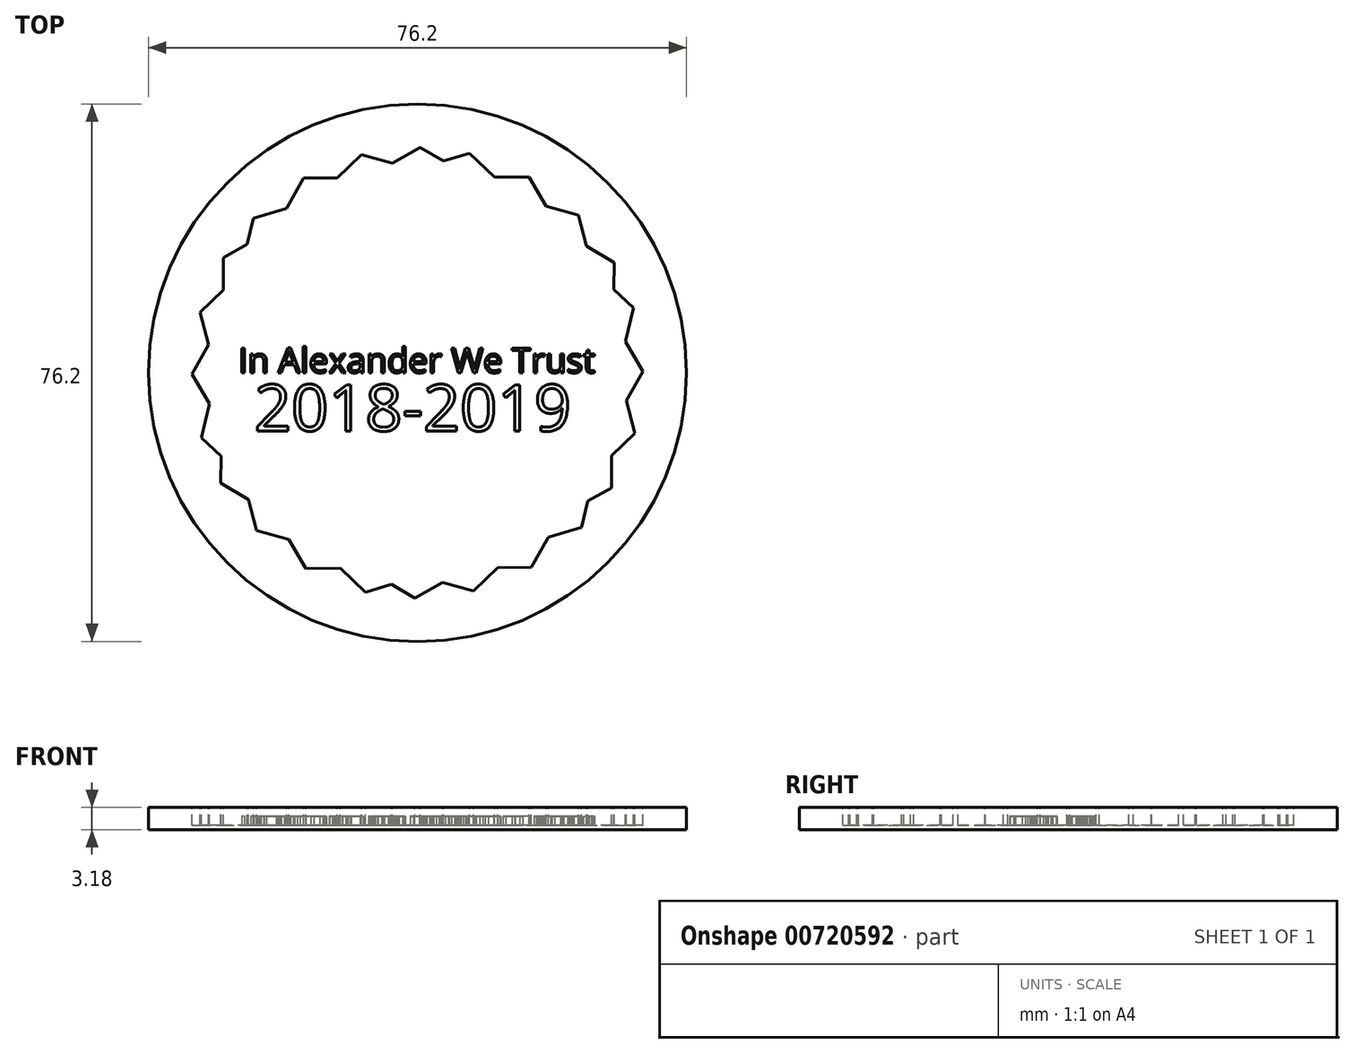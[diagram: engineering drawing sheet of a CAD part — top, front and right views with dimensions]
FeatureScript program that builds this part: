
annotation { "Feature Type Name" : "Feature", "Feature Type Description" : "" }
export const myFeature = defineFeature(function(context is Context, id is Id, definition is map)
    precondition{}
    {
        {
            var Q0;
            Q0=qCreatedBy(makeId("Top.planeOp"),FACE);
            var sketch = newSketch(context, id + "F0", { "sketchPlane" : qUnion([Q0])});
            skCircle(sketch, "E0", {"center": v(0, 0) * mm, "radius": 38.1 * mm});
            skSolve(sketch);
        }
        {
            var Q0;
            Q0=makeQuery(id+"F0.imprint","IMPRINT",FACE,{"disambiguationData":[TD([[makeQuery(id+"F0.imprint","IMPRINT",EDGE,{"derivedFrom":sQuery(id+"F0.wireOp",EDGE,"E0")}),1.0]])]});
            extrude(context, id + "F1", {"entities" : qUnion([Q0]), "depth" : 3.17 * mm, "offsetDistance" : 25.4 * mm});
        }
        {
            var Q0;
            Q0=makeQuery(id+"F1.opExtrude","CAP_FACE",FACE,{"disambiguationData":[OSD([sQuery(id+"F0.wireOp",EDGE,"E0")])],"isStart":false});
            var sketch = newSketch(context, id + "F2", { "sketchPlane" : qUnion([Q0])});
            skCircle(sketch, "E1", {"center": v(0, 0) * mm, "radius": 34.93 * mm});
            skCircle(sketch, "E2.cCircle", {"center": v(0, 0) * mm, "radius": 27.67 * mm, "construction": true});
            skLineSegment(sketch, "E2.0", {"start": v(15.83, 27.75) * mm, "end": v(31.95, 0.17) * mm});
            skLineSegment(sketch, "E2.1", {"start": v(31.95, 0.17) * mm, "end": v(16.12, -27.58) * mm});
            skLineSegment(sketch, "E2.2", {"start": v(16.12, -27.58) * mm, "end": v(-15.83, -27.75) * mm});
            skLineSegment(sketch, "E2.3", {"start": v(-15.83, -27.75) * mm, "end": v(-31.95, -0.17) * mm});
            skLineSegment(sketch, "E2.4", {"start": v(-31.95, -0.17) * mm, "end": v(-16.12, 27.58) * mm});
            skLineSegment(sketch, "E2.5", {"start": v(-16.12, 27.58) * mm, "end": v(15.83, 27.75) * mm});
            skPoint(sketch, "E2.0.midPoint", {"position": v(23.89, 13.96) * mm});
            skLineSegment(sketch, "E3.0", {"start": v(0.4, 31.95) * mm, "end": v(27.87, 15.63) * mm});
            skLineSegment(sketch, "E3.1", {"start": v(27.87, 15.63) * mm, "end": v(27.47, -16.32) * mm});
            skLineSegment(sketch, "E3.2", {"start": v(27.47, -16.32) * mm, "end": v(-0.4, -31.95) * mm});
            skLineSegment(sketch, "E3.3", {"start": v(-0.4, -31.95) * mm, "end": v(-27.87, -15.63) * mm});
            skLineSegment(sketch, "E3.4", {"start": v(-27.87, -15.63) * mm, "end": v(-27.47, 16.32) * mm});
            skLineSegment(sketch, "E3.5", {"start": v(-27.47, 16.32) * mm, "end": v(0.4, 31.95) * mm});
            skPoint(sketch, "E3.0.midPoint", {"position": v(14.13, 23.79) * mm});
            skLineSegment(sketch, "E4.0", {"start": v(22.82, 22.36) * mm, "end": v(30.78, -8.58) * mm});
            skLineSegment(sketch, "E4.1", {"start": v(30.78, -8.58) * mm, "end": v(7.96, -30.94) * mm});
            skLineSegment(sketch, "E4.2", {"start": v(7.96, -30.94) * mm, "end": v(-22.82, -22.36) * mm});
            skLineSegment(sketch, "E4.3", {"start": v(-22.82, -22.36) * mm, "end": v(-30.78, 8.58) * mm});
            skLineSegment(sketch, "E4.4", {"start": v(-30.78, 8.58) * mm, "end": v(-7.96, 30.94) * mm});
            skLineSegment(sketch, "E4.5", {"start": v(-7.96, 30.94) * mm, "end": v(22.82, 22.36) * mm});
            skPoint(sketch, "E4.0.midPoint", {"position": v(26.8, 6.9) * mm});
            skLineSegment(sketch, "E5.0", {"start": v(-23.26, 21.9) * mm, "end": v(7.34, 31.1) * mm});
            skLineSegment(sketch, "E5.1", {"start": v(7.34, 31.1) * mm, "end": v(30.6, 9.19) * mm});
            skLineSegment(sketch, "E5.2", {"start": v(30.6, 9.19) * mm, "end": v(23.26, -21.9) * mm});
            skLineSegment(sketch, "E5.3", {"start": v(23.26, -21.9) * mm, "end": v(-7.34, -31.1) * mm});
            skLineSegment(sketch, "E5.4", {"start": v(-7.34, -31.1) * mm, "end": v(-30.6, -9.19) * mm});
            skLineSegment(sketch, "E5.5", {"start": v(-30.6, -9.19) * mm, "end": v(-23.26, 21.9) * mm});
            skPoint(sketch, "E5.0.midPoint", {"position": v(-7.96, 26.5) * mm});
            skSolve(sketch);
        }
        {
            var Q0;
            {var subQ0=sQuery(id+"F2.wireOp",EDGE,"E4.2");var subQ1=sQuery(id+"F2.wireOp",EDGE,"E2.3");var subQ2=makeQuery(id+"F2.imprint","INTERSECT",VERTEX,{"derivedFrom":[subQ1,subQ0]});Q0=makeQuery(id+"F2.imprint","IMPRINT",FACE,{"disambiguationData":[TD([[makeQuery(id+"F2.imprint","IMPRINT",EDGE,{"disambiguationData":[TD([[subQ2,-1.0]])],"derivedFrom":subQ1}),-1.0]])]});}
            var Q1;
            {var subQ0=sQuery(id+"F2.wireOp",EDGE,"E2.3");var subQ1=sQuery(id+"F2.wireOp",EDGE,"E2.2");var subQ2=makeQuery(id+"F2.imprint","INTERSECT",VERTEX,{"derivedFrom":[subQ1,subQ0]});Q1=makeQuery(id+"F2.imprint","IMPRINT",FACE,{"disambiguationData":[TD([[makeQuery(id+"F2.imprint","IMPRINT",EDGE,{"disambiguationData":[TD([[subQ2,1.0]])],"derivedFrom":subQ1}),-1.0]])]});}
            var Q2;
            {var subQ0=sQuery(id+"F2.wireOp",EDGE,"E4.2");var subQ1=sQuery(id+"F2.wireOp",EDGE,"E2.2");var subQ2=makeQuery(id+"F2.imprint","INTERSECT",VERTEX,{"derivedFrom":[subQ1,subQ0]});Q2=makeQuery(id+"F2.imprint","IMPRINT",FACE,{"disambiguationData":[TD([[makeQuery(id+"F2.imprint","IMPRINT",EDGE,{"disambiguationData":[TD([[subQ2,-1.0]])],"derivedFrom":subQ1}),-1.0]])]});}
            var Q3;
            {var subQ0=sQuery(id+"F2.wireOp",EDGE,"E4.2");var subQ1=sQuery(id+"F2.wireOp",EDGE,"E2.2");var subQ2=makeQuery(id+"F2.imprint","INTERSECT",VERTEX,{"derivedFrom":[subQ1,subQ0]});Q3=makeQuery(id+"F2.imprint","IMPRINT",FACE,{"disambiguationData":[TD([[makeQuery(id+"F2.imprint","IMPRINT",EDGE,{"disambiguationData":[TD([[subQ2,-1.0]])],"derivedFrom":subQ1}),1.0]])]});}
            var Q4;
            {var subQ0=sQuery(id+"F2.wireOp",EDGE,"E3.2");var subQ1=sQuery(id+"F2.wireOp",EDGE,"E2.2");var subQ2=makeQuery(id+"F2.imprint","INTERSECT",VERTEX,{"derivedFrom":[subQ1,subQ0]});Q4=makeQuery(id+"F2.imprint","IMPRINT",FACE,{"disambiguationData":[TD([[makeQuery(id+"F2.imprint","IMPRINT",EDGE,{"disambiguationData":[TD([[subQ2,-1.0]])],"derivedFrom":subQ1}),1.0]])]});}
            var Q5;
            {var subQ0=sQuery(id+"F2.wireOp",EDGE,"E4.1");var subQ1=sQuery(id+"F2.wireOp",EDGE,"E2.2");var subQ2=makeQuery(id+"F2.imprint","INTERSECT",VERTEX,{"derivedFrom":[subQ1,subQ0]});Q5=makeQuery(id+"F2.imprint","IMPRINT",FACE,{"disambiguationData":[TD([[makeQuery(id+"F2.imprint","IMPRINT",EDGE,{"disambiguationData":[TD([[subQ2,-1.0]])],"derivedFrom":subQ1}),1.0]])]});}
            var Q6;
            {var subQ0=sQuery(id+"F2.wireOp",EDGE,"E4.1");var subQ1=sQuery(id+"F2.wireOp",EDGE,"E2.2");var subQ2=makeQuery(id+"F2.imprint","INTERSECT",VERTEX,{"derivedFrom":[subQ1,subQ0]});Q6=makeQuery(id+"F2.imprint","IMPRINT",FACE,{"disambiguationData":[TD([[makeQuery(id+"F2.imprint","IMPRINT",EDGE,{"disambiguationData":[TD([[subQ2,-1.0]])],"derivedFrom":subQ1}),-1.0]])]});}
            var Q7;
            {var subQ0=sQuery(id+"F2.wireOp",EDGE,"E2.2");var subQ1=sQuery(id+"F2.wireOp",EDGE,"E2.1");var subQ2=makeQuery(id+"F2.imprint","INTERSECT",VERTEX,{"derivedFrom":[subQ1,subQ0]});Q7=makeQuery(id+"F2.imprint","IMPRINT",FACE,{"disambiguationData":[TD([[makeQuery(id+"F2.imprint","IMPRINT",EDGE,{"disambiguationData":[TD([[subQ2,1.0]])],"derivedFrom":subQ1}),-1.0]])]});}
            var Q8;
            {var subQ15=sQuery(id+"F2.wireOp",EDGE,"E3.0");var subQ16=sQuery(id+"F2.wireOp",EDGE,"E2.0");var subQ17=makeQuery(id+"F2.imprint","INTERSECT",VERTEX,{"derivedFrom":[subQ16,subQ15]});Q8=makeQuery(id+"F2.imprint","IMPRINT",FACE,{"disambiguationData":[TD([[makeQuery(id+"F2.imprint","IMPRINT",EDGE,{"disambiguationData":[TD([[subQ17,-1.0]])],"derivedFrom":subQ16}),-1.0]])]});}
            var Q9;
            {var subQ0=sQuery(id+"F2.wireOp",EDGE,"E4.1");var subQ1=sQuery(id+"F2.wireOp",EDGE,"E2.1");var subQ2=makeQuery(id+"F2.imprint","INTERSECT",VERTEX,{"derivedFrom":[subQ1,subQ0]});Q9=makeQuery(id+"F2.imprint","IMPRINT",FACE,{"disambiguationData":[TD([[makeQuery(id+"F2.imprint","IMPRINT",EDGE,{"disambiguationData":[TD([[subQ2,-1.0]])],"derivedFrom":subQ1}),-1.0]])]});}
            var Q10;
            {var subQ0=sQuery(id+"F2.wireOp",EDGE,"E4.1");var subQ1=sQuery(id+"F2.wireOp",EDGE,"E2.1");var subQ2=makeQuery(id+"F2.imprint","INTERSECT",VERTEX,{"derivedFrom":[subQ1,subQ0]});Q10=makeQuery(id+"F2.imprint","IMPRINT",FACE,{"disambiguationData":[TD([[makeQuery(id+"F2.imprint","IMPRINT",EDGE,{"disambiguationData":[TD([[subQ2,-1.0]])],"derivedFrom":subQ1}),1.0]])]});}
            var Q11;
            {var subQ0=sQuery(id+"F2.wireOp",EDGE,"E3.1");var subQ1=sQuery(id+"F2.wireOp",EDGE,"E2.1");var subQ2=makeQuery(id+"F2.imprint","INTERSECT",VERTEX,{"derivedFrom":[subQ1,subQ0]});Q11=makeQuery(id+"F2.imprint","IMPRINT",FACE,{"disambiguationData":[TD([[makeQuery(id+"F2.imprint","IMPRINT",EDGE,{"disambiguationData":[TD([[subQ2,-1.0]])],"derivedFrom":subQ1}),1.0]])]});}
            var Q12;
            {var subQ0=sQuery(id+"F2.wireOp",EDGE,"E4.0");var subQ1=sQuery(id+"F2.wireOp",EDGE,"E2.1");var subQ2=makeQuery(id+"F2.imprint","INTERSECT",VERTEX,{"derivedFrom":[subQ1,subQ0]});Q12=makeQuery(id+"F2.imprint","IMPRINT",FACE,{"disambiguationData":[TD([[makeQuery(id+"F2.imprint","IMPRINT",EDGE,{"disambiguationData":[TD([[subQ2,-1.0]])],"derivedFrom":subQ1}),1.0]])]});}
            var Q13;
            {var subQ0=sQuery(id+"F2.wireOp",EDGE,"E4.0");var subQ1=sQuery(id+"F2.wireOp",EDGE,"E2.1");var subQ2=makeQuery(id+"F2.imprint","INTERSECT",VERTEX,{"derivedFrom":[subQ1,subQ0]});Q13=makeQuery(id+"F2.imprint","IMPRINT",FACE,{"disambiguationData":[TD([[makeQuery(id+"F2.imprint","IMPRINT",EDGE,{"disambiguationData":[TD([[subQ2,-1.0]])],"derivedFrom":subQ1}),-1.0]])]});}
            var Q14;
            {var subQ0=sQuery(id+"F2.wireOp",EDGE,"E2.1");var subQ1=sQuery(id+"F2.wireOp",EDGE,"E2.0");var subQ2=makeQuery(id+"F2.imprint","INTERSECT",VERTEX,{"derivedFrom":[subQ1,subQ0]});Q14=makeQuery(id+"F2.imprint","IMPRINT",FACE,{"disambiguationData":[TD([[makeQuery(id+"F2.imprint","IMPRINT",EDGE,{"disambiguationData":[TD([[subQ2,1.0]])],"derivedFrom":subQ1}),-1.0]])]});}
            var Q15;
            {var subQ0=sQuery(id+"F2.wireOp",EDGE,"E4.0");var subQ1=sQuery(id+"F2.wireOp",EDGE,"E2.0");var subQ2=makeQuery(id+"F2.imprint","INTERSECT",VERTEX,{"derivedFrom":[subQ1,subQ0]});Q15=makeQuery(id+"F2.imprint","IMPRINT",FACE,{"disambiguationData":[TD([[makeQuery(id+"F2.imprint","IMPRINT",EDGE,{"disambiguationData":[TD([[subQ2,-1.0]])],"derivedFrom":subQ1}),-1.0]])]});}
            var Q16;
            {var subQ0=sQuery(id+"F2.wireOp",EDGE,"E4.0");var subQ1=sQuery(id+"F2.wireOp",EDGE,"E2.0");var subQ2=makeQuery(id+"F2.imprint","INTERSECT",VERTEX,{"derivedFrom":[subQ1,subQ0]});Q16=makeQuery(id+"F2.imprint","IMPRINT",FACE,{"disambiguationData":[TD([[makeQuery(id+"F2.imprint","IMPRINT",EDGE,{"disambiguationData":[TD([[subQ2,-1.0]])],"derivedFrom":subQ1}),1.0]])]});}
            var Q17;
            {var subQ0=sQuery(id+"F2.wireOp",EDGE,"E3.0");var subQ1=sQuery(id+"F2.wireOp",EDGE,"E2.0");var subQ2=makeQuery(id+"F2.imprint","INTERSECT",VERTEX,{"derivedFrom":[subQ1,subQ0]});Q17=makeQuery(id+"F2.imprint","IMPRINT",FACE,{"disambiguationData":[TD([[makeQuery(id+"F2.imprint","IMPRINT",EDGE,{"disambiguationData":[TD([[subQ2,-1.0]])],"derivedFrom":subQ1}),1.0]])]});}
            var Q18;
            {var subQ0=sQuery(id+"F2.wireOp",EDGE,"E4.5");var subQ1=sQuery(id+"F2.wireOp",EDGE,"E2.0");var subQ2=makeQuery(id+"F2.imprint","INTERSECT",VERTEX,{"derivedFrom":[subQ1,subQ0]});Q18=makeQuery(id+"F2.imprint","IMPRINT",FACE,{"disambiguationData":[TD([[makeQuery(id+"F2.imprint","IMPRINT",EDGE,{"disambiguationData":[TD([[subQ2,-1.0]])],"derivedFrom":subQ1}),1.0]])]});}
            var Q19;
            {var subQ0=sQuery(id+"F2.wireOp",EDGE,"E4.5");var subQ1=sQuery(id+"F2.wireOp",EDGE,"E2.0");var subQ2=makeQuery(id+"F2.imprint","INTERSECT",VERTEX,{"derivedFrom":[subQ1,subQ0]});Q19=makeQuery(id+"F2.imprint","IMPRINT",FACE,{"disambiguationData":[TD([[makeQuery(id+"F2.imprint","IMPRINT",EDGE,{"disambiguationData":[TD([[subQ2,-1.0]])],"derivedFrom":subQ1}),-1.0]])]});}
            var Q20;
            {var subQ0=sQuery(id+"F2.wireOp",EDGE,"E2.5");var subQ1=sQuery(id+"F2.wireOp",EDGE,"E2.0");var subQ2=makeQuery(id+"F2.imprint","INTERSECT",VERTEX,{"derivedFrom":[subQ1,subQ0]});Q20=makeQuery(id+"F2.imprint","IMPRINT",FACE,{"disambiguationData":[TD([[makeQuery(id+"F2.imprint","IMPRINT",EDGE,{"disambiguationData":[TD([[subQ2,-1.0]])],"derivedFrom":subQ1}),-1.0]])]});}
            var Q21;
            {var subQ0=sQuery(id+"F2.wireOp",EDGE,"E4.5");var subQ1=sQuery(id+"F2.wireOp",EDGE,"E2.5");var subQ2=makeQuery(id+"F2.imprint","INTERSECT",VERTEX,{"derivedFrom":[subQ1,subQ0]});Q21=makeQuery(id+"F2.imprint","IMPRINT",FACE,{"disambiguationData":[TD([[makeQuery(id+"F2.imprint","IMPRINT",EDGE,{"disambiguationData":[TD([[subQ2,-1.0]])],"derivedFrom":subQ1}),1.0]])]});}
            var Q22;
            {var subQ0=sQuery(id+"F2.wireOp",EDGE,"E3.5");var subQ1=sQuery(id+"F2.wireOp",EDGE,"E2.5");var subQ2=makeQuery(id+"F2.imprint","INTERSECT",VERTEX,{"derivedFrom":[subQ1,subQ0]});Q22=makeQuery(id+"F2.imprint","IMPRINT",FACE,{"disambiguationData":[TD([[makeQuery(id+"F2.imprint","IMPRINT",EDGE,{"disambiguationData":[TD([[subQ2,-1.0]])],"derivedFrom":subQ1}),1.0]])]});}
            var Q23;
            {var subQ0=sQuery(id+"F2.wireOp",EDGE,"E4.5");var subQ1=sQuery(id+"F2.wireOp",EDGE,"E2.5");var subQ2=makeQuery(id+"F2.imprint","INTERSECT",VERTEX,{"derivedFrom":[subQ1,subQ0]});Q23=makeQuery(id+"F2.imprint","IMPRINT",FACE,{"disambiguationData":[TD([[makeQuery(id+"F2.imprint","IMPRINT",EDGE,{"disambiguationData":[TD([[subQ2,-1.0]])],"derivedFrom":subQ1}),-1.0]])]});}
            var Q24;
            {var subQ0=sQuery(id+"F2.wireOp",EDGE,"E4.4");var subQ1=sQuery(id+"F2.wireOp",EDGE,"E2.5");var subQ2=makeQuery(id+"F2.imprint","INTERSECT",VERTEX,{"derivedFrom":[subQ1,subQ0]});Q24=makeQuery(id+"F2.imprint","IMPRINT",FACE,{"disambiguationData":[TD([[makeQuery(id+"F2.imprint","IMPRINT",EDGE,{"disambiguationData":[TD([[subQ2,-1.0]])],"derivedFrom":subQ1}),-1.0]])]});}
            var Q25;
            {var subQ0=sQuery(id+"F2.wireOp",EDGE,"E4.4");var subQ1=sQuery(id+"F2.wireOp",EDGE,"E2.5");var subQ2=makeQuery(id+"F2.imprint","INTERSECT",VERTEX,{"derivedFrom":[subQ1,subQ0]});Q25=makeQuery(id+"F2.imprint","IMPRINT",FACE,{"disambiguationData":[TD([[makeQuery(id+"F2.imprint","IMPRINT",EDGE,{"disambiguationData":[TD([[subQ2,-1.0]])],"derivedFrom":subQ1}),1.0]])]});}
            var Q26;
            {var subQ0=sQuery(id+"F2.wireOp",EDGE,"E2.5");var subQ1=sQuery(id+"F2.wireOp",EDGE,"E2.4");var subQ2=makeQuery(id+"F2.imprint","INTERSECT",VERTEX,{"derivedFrom":[subQ1,subQ0]});Q26=makeQuery(id+"F2.imprint","IMPRINT",FACE,{"disambiguationData":[TD([[makeQuery(id+"F2.imprint","IMPRINT",EDGE,{"disambiguationData":[TD([[subQ2,1.0]])],"derivedFrom":subQ1}),-1.0]])]});}
            var Q27;
            {var subQ0=sQuery(id+"F2.wireOp",EDGE,"E4.4");var subQ1=sQuery(id+"F2.wireOp",EDGE,"E2.4");var subQ2=makeQuery(id+"F2.imprint","INTERSECT",VERTEX,{"derivedFrom":[subQ1,subQ0]});Q27=makeQuery(id+"F2.imprint","IMPRINT",FACE,{"disambiguationData":[TD([[makeQuery(id+"F2.imprint","IMPRINT",EDGE,{"disambiguationData":[TD([[subQ2,-1.0]])],"derivedFrom":subQ1}),-1.0]])]});}
            var Q28;
            {var subQ0=sQuery(id+"F2.wireOp",EDGE,"E4.4");var subQ1=sQuery(id+"F2.wireOp",EDGE,"E2.4");var subQ2=makeQuery(id+"F2.imprint","INTERSECT",VERTEX,{"derivedFrom":[subQ1,subQ0]});Q28=makeQuery(id+"F2.imprint","IMPRINT",FACE,{"disambiguationData":[TD([[makeQuery(id+"F2.imprint","IMPRINT",EDGE,{"disambiguationData":[TD([[subQ2,-1.0]])],"derivedFrom":subQ1}),1.0]])]});}
            var Q29;
            {var subQ0=sQuery(id+"F2.wireOp",EDGE,"E3.4");var subQ1=sQuery(id+"F2.wireOp",EDGE,"E2.4");var subQ2=makeQuery(id+"F2.imprint","INTERSECT",VERTEX,{"derivedFrom":[subQ1,subQ0]});Q29=makeQuery(id+"F2.imprint","IMPRINT",FACE,{"disambiguationData":[TD([[makeQuery(id+"F2.imprint","IMPRINT",EDGE,{"disambiguationData":[TD([[subQ2,-1.0]])],"derivedFrom":subQ1}),1.0]])]});}
            var Q30;
            {var subQ0=sQuery(id+"F2.wireOp",EDGE,"E4.3");var subQ1=sQuery(id+"F2.wireOp",EDGE,"E2.4");var subQ2=makeQuery(id+"F2.imprint","INTERSECT",VERTEX,{"derivedFrom":[subQ1,subQ0]});Q30=makeQuery(id+"F2.imprint","IMPRINT",FACE,{"disambiguationData":[TD([[makeQuery(id+"F2.imprint","IMPRINT",EDGE,{"disambiguationData":[TD([[subQ2,-1.0]])],"derivedFrom":subQ1}),1.0]])]});}
            var Q31;
            {var subQ0=sQuery(id+"F2.wireOp",EDGE,"E4.3");var subQ1=sQuery(id+"F2.wireOp",EDGE,"E2.4");var subQ2=makeQuery(id+"F2.imprint","INTERSECT",VERTEX,{"derivedFrom":[subQ1,subQ0]});Q31=makeQuery(id+"F2.imprint","IMPRINT",FACE,{"disambiguationData":[TD([[makeQuery(id+"F2.imprint","IMPRINT",EDGE,{"disambiguationData":[TD([[subQ2,-1.0]])],"derivedFrom":subQ1}),-1.0]])]});}
            var Q32;
            {var subQ0=sQuery(id+"F2.wireOp",EDGE,"E2.4");var subQ1=sQuery(id+"F2.wireOp",EDGE,"E2.3");var subQ2=makeQuery(id+"F2.imprint","INTERSECT",VERTEX,{"derivedFrom":[subQ1,subQ0]});Q32=makeQuery(id+"F2.imprint","IMPRINT",FACE,{"disambiguationData":[TD([[makeQuery(id+"F2.imprint","IMPRINT",EDGE,{"disambiguationData":[TD([[subQ2,1.0]])],"derivedFrom":subQ1}),-1.0]])]});}
            var Q33;
            {var subQ0=sQuery(id+"F2.wireOp",EDGE,"E4.3");var subQ1=sQuery(id+"F2.wireOp",EDGE,"E2.3");var subQ2=makeQuery(id+"F2.imprint","INTERSECT",VERTEX,{"derivedFrom":[subQ1,subQ0]});Q33=makeQuery(id+"F2.imprint","IMPRINT",FACE,{"disambiguationData":[TD([[makeQuery(id+"F2.imprint","IMPRINT",EDGE,{"disambiguationData":[TD([[subQ2,-1.0]])],"derivedFrom":subQ1}),-1.0]])]});}
            var Q34;
            {var subQ0=sQuery(id+"F2.wireOp",EDGE,"E3.3");var subQ1=sQuery(id+"F2.wireOp",EDGE,"E2.3");var subQ2=makeQuery(id+"F2.imprint","INTERSECT",VERTEX,{"derivedFrom":[subQ1,subQ0]});Q34=makeQuery(id+"F2.imprint","IMPRINT",FACE,{"disambiguationData":[TD([[makeQuery(id+"F2.imprint","IMPRINT",EDGE,{"disambiguationData":[TD([[subQ2,-1.0]])],"derivedFrom":subQ1}),1.0]])]});}
            var Q35;
            {var subQ0=sQuery(id+"F2.wireOp",EDGE,"E4.3");var subQ1=sQuery(id+"F2.wireOp",EDGE,"E2.3");var subQ2=makeQuery(id+"F2.imprint","INTERSECT",VERTEX,{"derivedFrom":[subQ1,subQ0]});Q35=makeQuery(id+"F2.imprint","IMPRINT",FACE,{"disambiguationData":[TD([[makeQuery(id+"F2.imprint","IMPRINT",EDGE,{"disambiguationData":[TD([[subQ2,-1.0]])],"derivedFrom":subQ1}),1.0]])]});}
            var Q36;
            {var subQ0=sQuery(id+"F2.wireOp",EDGE,"E3.4");var subQ1=sQuery(id+"F2.wireOp",EDGE,"E3.3");var subQ2=makeQuery(id+"F2.imprint","INTERSECT",VERTEX,{"derivedFrom":[subQ1,subQ0]});Q36=makeQuery(id+"F2.imprint","IMPRINT",FACE,{"disambiguationData":[TD([[makeQuery(id+"F2.imprint","IMPRINT",EDGE,{"disambiguationData":[TD([[subQ2,1.0]])],"derivedFrom":subQ1}),-1.0]])]});}
            var Q37;
            {var subQ0=sQuery(id+"F2.wireOp",EDGE,"E3.4");var subQ1=sQuery(id+"F2.wireOp",EDGE,"E2.3");var subQ2=makeQuery(id+"F2.imprint","INTERSECT",VERTEX,{"derivedFrom":[subQ1,subQ0]});Q37=makeQuery(id+"F2.imprint","IMPRINT",FACE,{"disambiguationData":[TD([[makeQuery(id+"F2.imprint","IMPRINT",EDGE,{"disambiguationData":[TD([[subQ2,-1.0]])],"derivedFrom":subQ1}),1.0]])]});}
            var Q38;
            {var subQ0=sQuery(id+"F2.wireOp",EDGE,"E3.4");var subQ1=sQuery(id+"F2.wireOp",EDGE,"E2.3");var subQ2=makeQuery(id+"F2.imprint","INTERSECT",VERTEX,{"derivedFrom":[subQ1,subQ0]});Q38=makeQuery(id+"F2.imprint","IMPRINT",FACE,{"disambiguationData":[TD([[makeQuery(id+"F2.imprint","IMPRINT",EDGE,{"disambiguationData":[TD([[subQ2,-1.0]])],"derivedFrom":subQ1}),-1.0]])]});}
            var Q39;
            {var subQ0=sQuery(id+"F2.wireOp",EDGE,"E4.3");var subQ1=sQuery(id+"F2.wireOp",EDGE,"E3.4");var subQ2=makeQuery(id+"F2.imprint","INTERSECT",VERTEX,{"derivedFrom":[subQ1,subQ0]});Q39=makeQuery(id+"F2.imprint","IMPRINT",FACE,{"disambiguationData":[TD([[makeQuery(id+"F2.imprint","IMPRINT",EDGE,{"disambiguationData":[TD([[subQ2,-1.0]])],"derivedFrom":subQ1}),1.0]])]});}
            var Q40;
            {var subQ0=sQuery(id+"F2.wireOp",EDGE,"E3.4");var subQ1=sQuery(id+"F2.wireOp",EDGE,"E2.4");var subQ2=makeQuery(id+"F2.imprint","INTERSECT",VERTEX,{"derivedFrom":[subQ1,subQ0]});Q40=makeQuery(id+"F2.imprint","IMPRINT",FACE,{"disambiguationData":[TD([[makeQuery(id+"F2.imprint","IMPRINT",EDGE,{"disambiguationData":[TD([[subQ2,-1.0]])],"derivedFrom":subQ1}),-1.0]])]});}
            var Q41;
            {var subQ0=sQuery(id+"F2.wireOp",EDGE,"E5.5");var subQ1=sQuery(id+"F2.wireOp",EDGE,"E2.4");var subQ2=makeQuery(id+"F2.imprint","INTERSECT",VERTEX,{"derivedFrom":[subQ1,subQ0]});Q41=makeQuery(id+"F2.imprint","IMPRINT",FACE,{"disambiguationData":[TD([[makeQuery(id+"F2.imprint","IMPRINT",EDGE,{"disambiguationData":[TD([[subQ2,-1.0]])],"derivedFrom":subQ1}),1.0]])]});}
            var Q42;
            {var subQ0=sQuery(id+"F2.wireOp",EDGE,"E3.5");var subQ1=sQuery(id+"F2.wireOp",EDGE,"E3.4");var subQ2=makeQuery(id+"F2.imprint","INTERSECT",VERTEX,{"derivedFrom":[subQ1,subQ0]});Q42=makeQuery(id+"F2.imprint","IMPRINT",FACE,{"disambiguationData":[TD([[makeQuery(id+"F2.imprint","IMPRINT",EDGE,{"disambiguationData":[TD([[subQ2,1.0]])],"derivedFrom":subQ1}),-1.0]])]});}
            var Q43;
            {var subQ0=sQuery(id+"F2.wireOp",EDGE,"E3.5");var subQ1=sQuery(id+"F2.wireOp",EDGE,"E2.4");var subQ2=makeQuery(id+"F2.imprint","INTERSECT",VERTEX,{"derivedFrom":[subQ1,subQ0]});Q43=makeQuery(id+"F2.imprint","IMPRINT",FACE,{"disambiguationData":[TD([[makeQuery(id+"F2.imprint","IMPRINT",EDGE,{"disambiguationData":[TD([[subQ2,-1.0]])],"derivedFrom":subQ1}),1.0]])]});}
            var Q44;
            {var subQ0=sQuery(id+"F2.wireOp",EDGE,"E3.0");var subQ1=sQuery(id+"F2.wireOp",EDGE,"E2.5");var subQ2=makeQuery(id+"F2.imprint","INTERSECT",VERTEX,{"derivedFrom":[subQ1,subQ0]});Q44=makeQuery(id+"F2.imprint","IMPRINT",FACE,{"disambiguationData":[TD([[makeQuery(id+"F2.imprint","IMPRINT",EDGE,{"disambiguationData":[TD([[subQ2,-1.0]])],"derivedFrom":subQ1}),1.0]])]});}
            var Q45;
            {var subQ0=sQuery(id+"F2.wireOp",EDGE,"E3.5");var subQ1=sQuery(id+"F2.wireOp",EDGE,"E3.0");var subQ2=makeQuery(id+"F2.imprint","INTERSECT",VERTEX,{"derivedFrom":[subQ1,subQ0]});Q45=makeQuery(id+"F2.imprint","IMPRINT",FACE,{"disambiguationData":[TD([[makeQuery(id+"F2.imprint","IMPRINT",EDGE,{"disambiguationData":[TD([[subQ2,-1.0]])],"derivedFrom":subQ1}),-1.0]])]});}
            var Q46;
            {var subQ0=sQuery(id+"F2.wireOp",EDGE,"E5.0");var subQ1=sQuery(id+"F2.wireOp",EDGE,"E2.5");var subQ2=makeQuery(id+"F2.imprint","INTERSECT",VERTEX,{"derivedFrom":[subQ1,subQ0]});Q46=makeQuery(id+"F2.imprint","IMPRINT",FACE,{"disambiguationData":[TD([[makeQuery(id+"F2.imprint","IMPRINT",EDGE,{"disambiguationData":[TD([[subQ2,-1.0]])],"derivedFrom":subQ1}),1.0]])]});}
            var Q47;
            {var subQ0=sQuery(id+"F2.wireOp",EDGE,"E3.5");var subQ1=sQuery(id+"F2.wireOp",EDGE,"E2.5");var subQ2=makeQuery(id+"F2.imprint","INTERSECT",VERTEX,{"derivedFrom":[subQ1,subQ0]});Q47=makeQuery(id+"F2.imprint","IMPRINT",FACE,{"disambiguationData":[TD([[makeQuery(id+"F2.imprint","IMPRINT",EDGE,{"disambiguationData":[TD([[subQ2,-1.0]])],"derivedFrom":subQ1}),-1.0]])]});}
            var Q48;
            {var subQ0=sQuery(id+"F2.wireOp",EDGE,"E3.5");var subQ1=sQuery(id+"F2.wireOp",EDGE,"E2.4");var subQ2=makeQuery(id+"F2.imprint","INTERSECT",VERTEX,{"derivedFrom":[subQ1,subQ0]});Q48=makeQuery(id+"F2.imprint","IMPRINT",FACE,{"disambiguationData":[TD([[makeQuery(id+"F2.imprint","IMPRINT",EDGE,{"disambiguationData":[TD([[subQ2,-1.0]])],"derivedFrom":subQ1}),-1.0]])]});}
            var Q49;
            {var subQ0=sQuery(id+"F2.wireOp",EDGE,"E3.1");var subQ1=sQuery(id+"F2.wireOp",EDGE,"E2.0");var subQ2=makeQuery(id+"F2.imprint","INTERSECT",VERTEX,{"derivedFrom":[subQ1,subQ0]});Q49=makeQuery(id+"F2.imprint","IMPRINT",FACE,{"disambiguationData":[TD([[makeQuery(id+"F2.imprint","IMPRINT",EDGE,{"disambiguationData":[TD([[subQ2,-1.0]])],"derivedFrom":subQ1}),1.0]])]});}
            var Q50;
            {var subQ0=sQuery(id+"F2.wireOp",EDGE,"E3.1");var subQ1=sQuery(id+"F2.wireOp",EDGE,"E3.0");var subQ2=makeQuery(id+"F2.imprint","INTERSECT",VERTEX,{"derivedFrom":[subQ1,subQ0]});Q50=makeQuery(id+"F2.imprint","IMPRINT",FACE,{"disambiguationData":[TD([[makeQuery(id+"F2.imprint","IMPRINT",EDGE,{"disambiguationData":[TD([[subQ2,1.0]])],"derivedFrom":subQ1}),-1.0]])]});}
            var Q51;
            {var subQ0=sQuery(id+"F2.wireOp",EDGE,"E3.1");var subQ1=sQuery(id+"F2.wireOp",EDGE,"E2.0");var subQ2=makeQuery(id+"F2.imprint","INTERSECT",VERTEX,{"derivedFrom":[subQ1,subQ0]});Q51=makeQuery(id+"F2.imprint","IMPRINT",FACE,{"disambiguationData":[TD([[makeQuery(id+"F2.imprint","IMPRINT",EDGE,{"disambiguationData":[TD([[subQ2,-1.0]])],"derivedFrom":subQ1}),-1.0]])]});}
            var Q52;
            {var subQ0=sQuery(id+"F2.wireOp",EDGE,"E3.2");var subQ1=sQuery(id+"F2.wireOp",EDGE,"E3.1");var subQ2=makeQuery(id+"F2.imprint","INTERSECT",VERTEX,{"derivedFrom":[subQ1,subQ0]});Q52=makeQuery(id+"F2.imprint","IMPRINT",FACE,{"disambiguationData":[TD([[makeQuery(id+"F2.imprint","IMPRINT",EDGE,{"disambiguationData":[TD([[subQ2,1.0]])],"derivedFrom":subQ1}),-1.0]])]});}
            var Q53;
            {var subQ0=sQuery(id+"F2.wireOp",EDGE,"E3.2");var subQ1=sQuery(id+"F2.wireOp",EDGE,"E2.1");var subQ2=makeQuery(id+"F2.imprint","INTERSECT",VERTEX,{"derivedFrom":[subQ1,subQ0]});Q53=makeQuery(id+"F2.imprint","IMPRINT",FACE,{"disambiguationData":[TD([[makeQuery(id+"F2.imprint","IMPRINT",EDGE,{"disambiguationData":[TD([[subQ2,-1.0]])],"derivedFrom":subQ1}),1.0]])]});}
            var Q54;
            {var subQ0=sQuery(id+"F2.wireOp",EDGE,"E3.2");var subQ1=sQuery(id+"F2.wireOp",EDGE,"E2.1");var subQ2=makeQuery(id+"F2.imprint","INTERSECT",VERTEX,{"derivedFrom":[subQ1,subQ0]});Q54=makeQuery(id+"F2.imprint","IMPRINT",FACE,{"disambiguationData":[TD([[makeQuery(id+"F2.imprint","IMPRINT",EDGE,{"disambiguationData":[TD([[subQ2,-1.0]])],"derivedFrom":subQ1}),-1.0]])]});}
            var Q55;
            {var subQ0=sQuery(id+"F2.wireOp",EDGE,"E3.3");var subQ1=sQuery(id+"F2.wireOp",EDGE,"E3.2");var subQ2=makeQuery(id+"F2.imprint","INTERSECT",VERTEX,{"derivedFrom":[subQ1,subQ0]});Q55=makeQuery(id+"F2.imprint","IMPRINT",FACE,{"disambiguationData":[TD([[makeQuery(id+"F2.imprint","IMPRINT",EDGE,{"disambiguationData":[TD([[subQ2,1.0]])],"derivedFrom":subQ1}),-1.0]])]});}
            var Q56;
            {var subQ0=sQuery(id+"F2.wireOp",EDGE,"E3.3");var subQ1=sQuery(id+"F2.wireOp",EDGE,"E2.2");var subQ2=makeQuery(id+"F2.imprint","INTERSECT",VERTEX,{"derivedFrom":[subQ1,subQ0]});Q56=makeQuery(id+"F2.imprint","IMPRINT",FACE,{"disambiguationData":[TD([[makeQuery(id+"F2.imprint","IMPRINT",EDGE,{"disambiguationData":[TD([[subQ2,-1.0]])],"derivedFrom":subQ1}),1.0]])]});}
            var Q57;
            {var subQ0=sQuery(id+"F2.wireOp",EDGE,"E3.3");var subQ1=sQuery(id+"F2.wireOp",EDGE,"E2.2");var subQ2=makeQuery(id+"F2.imprint","INTERSECT",VERTEX,{"derivedFrom":[subQ1,subQ0]});Q57=makeQuery(id+"F2.imprint","IMPRINT",FACE,{"disambiguationData":[TD([[makeQuery(id+"F2.imprint","IMPRINT",EDGE,{"disambiguationData":[TD([[subQ2,-1.0]])],"derivedFrom":subQ1}),-1.0]])]});}
            var Q58;
            {var subQ0=sQuery(id+"F2.wireOp",EDGE,"E3.0");var subQ1=sQuery(id+"F2.wireOp",EDGE,"E2.5");var subQ2=makeQuery(id+"F2.imprint","INTERSECT",VERTEX,{"derivedFrom":[subQ1,subQ0]});Q58=makeQuery(id+"F2.imprint","IMPRINT",FACE,{"disambiguationData":[TD([[makeQuery(id+"F2.imprint","IMPRINT",EDGE,{"disambiguationData":[TD([[subQ2,-1.0]])],"derivedFrom":subQ1}),-1.0]])]});}
            var Q59;
            {var subQ10=sQuery(id+"F2.wireOp",EDGE,"E5.1");var subQ11=sQuery(id+"F2.wireOp",EDGE,"E2.0");var subQ12=makeQuery(id+"F2.imprint","INTERSECT",VERTEX,{"derivedFrom":[subQ11,subQ10]});Q59=makeQuery(id+"F2.imprint","IMPRINT",FACE,{"disambiguationData":[TD([[makeQuery(id+"F2.imprint","IMPRINT",EDGE,{"disambiguationData":[TD([[subQ12,-1.0]])],"derivedFrom":subQ11}),-1.0]])]});}
            var Q60;
            {var subQ0=sQuery(id+"F2.wireOp",EDGE,"E3.1");var subQ1=sQuery(id+"F2.wireOp",EDGE,"E2.1");var subQ2=makeQuery(id+"F2.imprint","INTERSECT",VERTEX,{"derivedFrom":[subQ1,subQ0]});Q60=makeQuery(id+"F2.imprint","IMPRINT",FACE,{"disambiguationData":[TD([[makeQuery(id+"F2.imprint","IMPRINT",EDGE,{"disambiguationData":[TD([[subQ2,-1.0]])],"derivedFrom":subQ1}),-1.0]])]});}
            var Q61;
            {var subQ0=sQuery(id+"F2.wireOp",EDGE,"E5.2");var subQ1=sQuery(id+"F2.wireOp",EDGE,"E2.1");var subQ2=makeQuery(id+"F2.imprint","INTERSECT",VERTEX,{"derivedFrom":[subQ1,subQ0]});Q61=makeQuery(id+"F2.imprint","IMPRINT",FACE,{"disambiguationData":[TD([[makeQuery(id+"F2.imprint","IMPRINT",EDGE,{"disambiguationData":[TD([[subQ2,-1.0]])],"derivedFrom":subQ1}),1.0]])]});}
            var Q62;
            {var subQ0=sQuery(id+"F2.wireOp",EDGE,"E3.2");var subQ1=sQuery(id+"F2.wireOp",EDGE,"E2.2");var subQ2=makeQuery(id+"F2.imprint","INTERSECT",VERTEX,{"derivedFrom":[subQ1,subQ0]});Q62=makeQuery(id+"F2.imprint","IMPRINT",FACE,{"disambiguationData":[TD([[makeQuery(id+"F2.imprint","IMPRINT",EDGE,{"disambiguationData":[TD([[subQ2,-1.0]])],"derivedFrom":subQ1}),-1.0]])]});}
            var Q63;
            {var subQ0=sQuery(id+"F2.wireOp",EDGE,"E4.1");var subQ1=sQuery(id+"F2.wireOp",EDGE,"E3.2");var subQ2=makeQuery(id+"F2.imprint","INTERSECT",VERTEX,{"derivedFrom":[subQ1,subQ0]});Q63=makeQuery(id+"F2.imprint","IMPRINT",FACE,{"disambiguationData":[TD([[makeQuery(id+"F2.imprint","IMPRINT",EDGE,{"disambiguationData":[TD([[subQ2,-1.0]])],"derivedFrom":subQ1}),1.0]])]});}
            var Q64;
            {var subQ0=sQuery(id+"F2.wireOp",EDGE,"E5.3");var subQ1=sQuery(id+"F2.wireOp",EDGE,"E2.2");var subQ2=makeQuery(id+"F2.imprint","INTERSECT",VERTEX,{"derivedFrom":[subQ1,subQ0]});Q64=makeQuery(id+"F2.imprint","IMPRINT",FACE,{"disambiguationData":[TD([[makeQuery(id+"F2.imprint","IMPRINT",EDGE,{"disambiguationData":[TD([[subQ2,-1.0]])],"derivedFrom":subQ1}),1.0]])]});}
            var Q65;
            {var subQ0=sQuery(id+"F2.wireOp",EDGE,"E4.2");var subQ1=sQuery(id+"F2.wireOp",EDGE,"E3.3");var subQ2=makeQuery(id+"F2.imprint","INTERSECT",VERTEX,{"derivedFrom":[subQ1,subQ0]});Q65=makeQuery(id+"F2.imprint","IMPRINT",FACE,{"disambiguationData":[TD([[makeQuery(id+"F2.imprint","IMPRINT",EDGE,{"disambiguationData":[TD([[subQ2,-1.0]])],"derivedFrom":subQ1}),1.0]])]});}
            var Q66;
            {var subQ0=sQuery(id+"F2.wireOp",EDGE,"E4.2");var subQ1=sQuery(id+"F2.wireOp",EDGE,"E2.3");var subQ2=makeQuery(id+"F2.imprint","INTERSECT",VERTEX,{"derivedFrom":[subQ1,subQ0]});Q66=makeQuery(id+"F2.imprint","IMPRINT",FACE,{"disambiguationData":[TD([[makeQuery(id+"F2.imprint","IMPRINT",EDGE,{"disambiguationData":[TD([[subQ2,-1.0]])],"derivedFrom":subQ1}),1.0]])]});}
            var Q67;
            {var subQ0=sQuery(id+"F2.wireOp",EDGE,"E5.4");var subQ1=sQuery(id+"F2.wireOp",EDGE,"E2.3");var subQ2=makeQuery(id+"F2.imprint","INTERSECT",VERTEX,{"derivedFrom":[subQ1,subQ0]});Q67=makeQuery(id+"F2.imprint","IMPRINT",FACE,{"disambiguationData":[TD([[makeQuery(id+"F2.imprint","IMPRINT",EDGE,{"disambiguationData":[TD([[subQ2,-1.0]])],"derivedFrom":subQ1}),1.0]])]});}
            var Q68;
            {var subQ0=sQuery(id+"F2.wireOp",EDGE,"E3.3");var subQ1=sQuery(id+"F2.wireOp",EDGE,"E2.3");var subQ2=makeQuery(id+"F2.imprint","INTERSECT",VERTEX,{"derivedFrom":[subQ1,subQ0]});Q68=makeQuery(id+"F2.imprint","IMPRINT",FACE,{"disambiguationData":[TD([[makeQuery(id+"F2.imprint","IMPRINT",EDGE,{"disambiguationData":[TD([[subQ2,-1.0]])],"derivedFrom":subQ1}),-1.0]])]});}
            var Q69;
            {var subQ0=sQuery(id+"F2.wireOp",EDGE,"E4.5");var subQ1=sQuery(id+"F2.wireOp",EDGE,"E3.0");var subQ2=makeQuery(id+"F2.imprint","INTERSECT",VERTEX,{"derivedFrom":[subQ1,subQ0]});Q69=makeQuery(id+"F2.imprint","IMPRINT",FACE,{"disambiguationData":[TD([[makeQuery(id+"F2.imprint","IMPRINT",EDGE,{"disambiguationData":[TD([[subQ2,-1.0]])],"derivedFrom":subQ1}),1.0]])]});}
            var Q70;
            {var subQ0=sQuery(id+"F2.wireOp",EDGE,"E4.4");var subQ1=sQuery(id+"F2.wireOp",EDGE,"E3.5");var subQ2=makeQuery(id+"F2.imprint","INTERSECT",VERTEX,{"derivedFrom":[subQ1,subQ0]});Q70=makeQuery(id+"F2.imprint","IMPRINT",FACE,{"disambiguationData":[TD([[makeQuery(id+"F2.imprint","IMPRINT",EDGE,{"disambiguationData":[TD([[subQ2,-1.0]])],"derivedFrom":subQ1}),1.0]])]});}
            var Q71;
            {var subQ0=sQuery(id+"F2.wireOp",EDGE,"E5.1");var subQ1=sQuery(id+"F2.wireOp",EDGE,"E2.0");var subQ2=makeQuery(id+"F2.imprint","INTERSECT",VERTEX,{"derivedFrom":[subQ1,subQ0]});Q71=makeQuery(id+"F2.imprint","IMPRINT",FACE,{"disambiguationData":[TD([[makeQuery(id+"F2.imprint","IMPRINT",EDGE,{"disambiguationData":[TD([[subQ2,-1.0]])],"derivedFrom":subQ1}),1.0]])]});}
            var Q72;
            {var subQ0=sQuery(id+"F2.wireOp",EDGE,"E4.0");var subQ1=sQuery(id+"F2.wireOp",EDGE,"E3.1");var subQ2=makeQuery(id+"F2.imprint","INTERSECT",VERTEX,{"derivedFrom":[subQ1,subQ0]});Q72=makeQuery(id+"F2.imprint","IMPRINT",FACE,{"disambiguationData":[TD([[makeQuery(id+"F2.imprint","IMPRINT",EDGE,{"disambiguationData":[TD([[subQ2,-1.0]])],"derivedFrom":subQ1}),1.0]])]});}
            extrude(context, id + "F3", {"entities" : qUnion([Q0, Q1, Q2, Q3, Q4, Q5, Q6, Q7, Q8, Q9, Q10, Q11, Q12, Q13, Q14, Q15, Q16, Q17, Q18, Q19, Q20, Q21, Q22, Q23, Q24, Q25, Q26, Q27, Q28, Q29, Q30, Q31, Q32, Q33, Q34, Q35, Q36, Q37, Q38, Q39, Q40, Q41, Q42, Q43, Q44, Q45, Q46, Q47, Q48, Q49, Q50, Q51, Q52, Q53, Q54, Q55, Q56, Q57, Q58, Q59, Q60, Q61, Q62, Q63, Q64, Q65, Q66, Q67, Q68, Q69, Q70, Q71, Q72]), "operationType" : NewBodyOperationType.REMOVE, "oppositeDirection" : true, "depth" : 2.54 * mm, "offsetDistance" : 25.4 * mm});
        }
        {
            var Q0;
            Q0=makeQuery(id+"F3.boolean.opBoolean","COPY",FACE,{"derivedFrom":makeQuery(id+"F3.opExtrude","CAP_FACE",FACE,{"disambiguationData":[OSD([sQuery(id+"F2.wireOp",EDGE,"E2.0"),sQuery(id+"F2.wireOp",EDGE,"E2.1"),sQuery(id+"F2.wireOp",EDGE,"E2.2"),sQuery(id+"F2.wireOp",EDGE,"E2.3"),sQuery(id+"F2.wireOp",EDGE,"E2.4"),sQuery(id+"F2.wireOp",EDGE,"E2.5"),sQuery(id+"F2.wireOp",EDGE,"E3.0"),sQuery(id+"F2.wireOp",EDGE,"E3.1"),sQuery(id+"F2.wireOp",EDGE,"E3.2"),sQuery(id+"F2.wireOp",EDGE,"E3.3"),sQuery(id+"F2.wireOp",EDGE,"E3.4"),sQuery(id+"F2.wireOp",EDGE,"E3.5"),sQuery(id+"F2.wireOp",EDGE,"E4.0"),sQuery(id+"F2.wireOp",EDGE,"E4.1"),sQuery(id+"F2.wireOp",EDGE,"E4.2"),sQuery(id+"F2.wireOp",EDGE,"E4.3"),sQuery(id+"F2.wireOp",EDGE,"E4.4"),sQuery(id+"F2.wireOp",EDGE,"E4.5")])],"isStart":false})});
            var sketch = newSketch(context, id + "F4", { "sketchPlane" : qUnion([Q0])});
            skText(sketch, "E6", { "text": "In Alexander We Trust", "fontName": "OpenSans-Regular.ttf"});
            skText(sketch, "E7", { "text": "2018-2019\n", "fontName": "OpenSans-Regular.ttf"});
            const initialGuessF4  = {"E6": [-0.0254, 0, 1, 0, 0.00354], "E7": [-0.02312, -0.00824, 1, 0, 0.0066]};
            skSetInitialGuess(sketch, initialGuessF4);
            skSolve(sketch);
        }
        {
            var Q0;
            Q0 = qSketchRegion(id + "F4", true);
            extrude(context, id + "F5", {"entities" : qUnion([Q0]), "operationType" : NewBodyOperationType.ADD, "depth" : 1.27 * mm, "offsetDistance" : 25.4 * mm});
        }
    });
